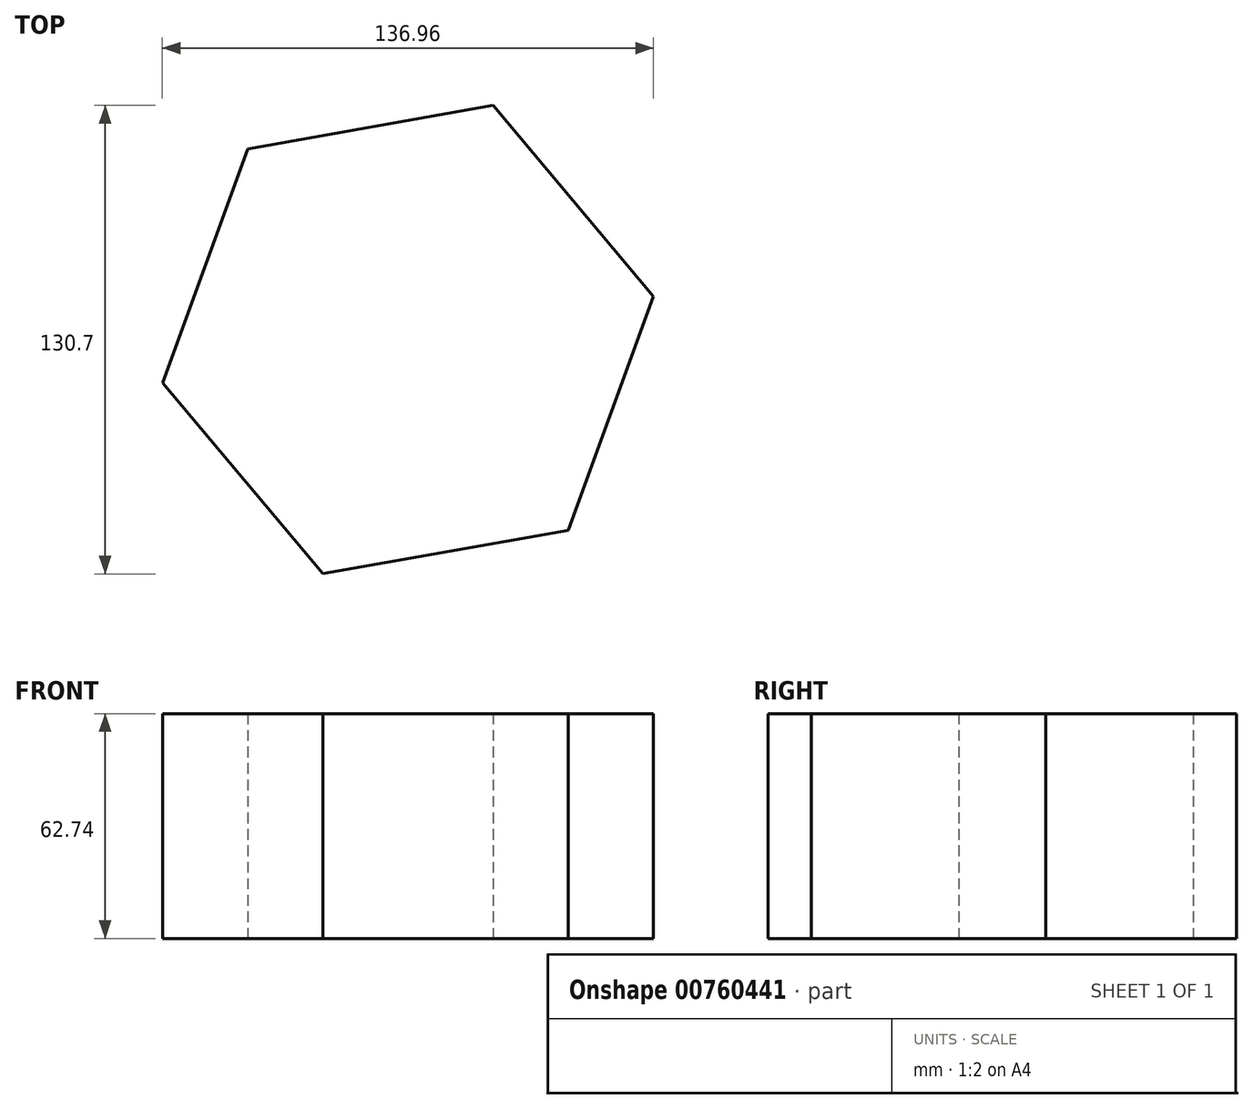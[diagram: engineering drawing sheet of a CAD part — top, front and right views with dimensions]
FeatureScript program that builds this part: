
annotation { "Feature Type Name" : "Feature", "Feature Type Description" : "" }
export const myFeature = defineFeature(function(context is Context, id is Id, definition is map)
    precondition{}
    {
        {
            var Q0;
            Q0=qCreatedBy(makeId("Top.planeOp"),FACE);
            var sketch = newSketch(context, id + "F0", { "sketchPlane" : qUnion([Q0])});
            skCircle(sketch, "E0.cCircle", {"center": v(0, 0) * mm, "radius": 60.22 * mm, "construction": true});
            skLineSegment(sketch, "E0.0", {"start": v(-23.77, -65.35) * mm, "end": v(-68.48, -12.1) * mm});
            skLineSegment(sketch, "E0.1", {"start": v(-68.48, -12.1) * mm, "end": v(-44.7, 53.26) * mm});
            skLineSegment(sketch, "E0.2", {"start": v(-44.7, 53.26) * mm, "end": v(23.77, 65.35) * mm});
            skLineSegment(sketch, "E0.3", {"start": v(23.77, 65.35) * mm, "end": v(68.48, 12.1) * mm});
            skLineSegment(sketch, "E0.4", {"start": v(68.48, 12.1) * mm, "end": v(44.7, -53.26) * mm});
            skLineSegment(sketch, "E0.5", {"start": v(44.7, -53.26) * mm, "end": v(-23.77, -65.35) * mm});
            skPoint(sketch, "E0.0.midPoint", {"position": v(-46.12, -38.72) * mm});
            skSolve(sketch);
        }
        {
            var Q0;
            Q0=makeQuery(id+"F0.imprint","IMPRINT",FACE,{"disambiguationData":[TD([[makeQuery(id+"F0.imprint","IMPRINT",EDGE,{"derivedFrom":sQuery(id+"F0.wireOp",EDGE,"E0.0")}),-1.0]])]});
            extrude(context, id + "F1", {"entities" : qUnion([Q0]), "depth" : 62.74 * mm, "offsetDistance" : 25.4 * mm});
        }
    });
